# Revit family: IS_Iom_A7925_BIM_NL
name_source: partatom
category: Plumbing Fixtures
units: mm (PartAtom-declared; Revit-internal decimal feet)

## family parameters
Always vertical = No
Cut with Voids When Loaded = No
OmniClass Number = 23.45.05.14.21.11
OmniClass Title = Bath/Shower Units
Part Type = Normal
Room Calculation Point = No
Round Connector Dimension = Use Diameter
Shared = No
Work Plane-Based = No

## types (5) — shared parameters
Accessories = http://www.idealstandard.nl
Afmetingen = 76 x 107 x 218 mm
AfstandsEenheid = Millimeter
AreaUnits = millimetres
AssetType = Fixed
Auteur = Ideal Standard
BIMObjectName = IS_IdealStandard_SanitaryAccessories_IOM_A7925
BIMobject category = Sanitary: Toilet Accssories
BIMobject main category = Sanitary
BIMobject main category code = Sanitary
Beschrijvinggarantie = Herstellergarantie
Bestanddelen = http://www.idealstandard.nl
BimObjectNaam = IS_IdealStandard_SanitaryAccessories_IOM_A7925
Brand = Ideal Standard
Brand url = http://www.idealstandard.nl
Breedte = 76.032108
Category = Plumbing
Classification = Sanitary
ConnectionType = Plumbing
CurrencyUnit = €
CurrentRevision = 1
Date of publishing = 24/01/2023
Diepte = 107 mm
DurationUnit = Years
DuurEenheid = Jahr
Edition number = 1
ElementType = Sanitary Accessories
Garantieunits = Jahre
GemaaktOp = 24/01/2023
Help = http://www.idealstandard.nl
Hoogte = 218.007999420166
IFC Classification = Sanitary Terminal
IfcExportAs = IfcFurnitureType
IfcExportType = SOAP DISPENSER
Installatieinstructies = http://www.idealstandard.nl
Installation instructions = http://www.idealstandard.nl
InstallationInstructions = http://www.idealstandard.nl
Lengte = 107 mm
LinearUnits = millimeters
MaintenanceInformation = http://www.idealstandard.nl
Manufacturer = Ideal Standard
Manufacturer name = Ideal Standard
ManufacturerURL = http://www.idealstandard.nl
Materiaal = Messing&Stahl
Material = brass&steel
Material main = brass&steel
Merk = Ideal Standard
ModelReference = Iom Lotion Dispencer Wall Mounted
NBS Reference Code = 45-35-72/358
NBS Reference Description = Soap dispensers
Name = SanitaryAccessories_IOM_A7925_IdealStandard
NettWeight = 0.001
Nettogewicht = 0.001
NominalDepth = 107 mm
NominalHeight = 218 mm
NominalLength = 107 mm
NominalWidth = 76 mm
OppervlakteAfmeting = Millimeter
OppervlakteEenheid = Millimeter
PredefinedType = Sanitary Accessories
Product Guid = 11c9dca1-c7c1-4e85-bdf3-611bfd7340cd
Product SKU = A7925
Product certification = http://www.idealstandard.nl
Product data url = https://bimobject.com
Product family = Iom
Product group = Accessories
Product name = Iom Lotion Dispencer Wall Mounted
Product url = http://www.idealstandard.nl
ProductInformation = http://www.idealstandard.nl
Productinformatie = http://www.idealstandard.nl
QR code = http://bimobject.com
Revisie = 1
Shape = cilindrical
Size = 76 x 107 x 218 mm
Space = Internal
SpareParts = http://www.idealstandard.nl
Technical description = http://www.idealstandard.nl
Telefoonnummer = 077 355 08 08
Typeconnectie = Installation
UNSPSC Code = 30181500
URL = http://www.idealstandard.nl
Uniclass 1.4 Code = N14
Uniclass 1.4 Description = Accessories
Uniclass 2015 Code = Pr_40_20_76
Uniclass 2015 Name = Sanitary accessories
Uniclass2015Beschrijving = Sanitary accessories
Uniclass2015Code = Pr_40_20_76
Uniclass2015Referentie = Sanitary accessories
Uniclass2015Title = Sanitary accessories
Uniclass2015Version = V1.26
Uniformat II Code = C1030
Uniformat II Description = Fittings
Urlproducent = http://www.idealstandard.nl
ValutaEenheid = €
Versie = 1
Version = 1
VolumeUnits = Liters
Volumeunits = Liter
Vorm = Zylinder
WRASURL = https://www.wrasapprovals.co.uk
WarrantyDescription = Manufacturers Warranty
WarrantyDurationUnit = Years
Weight Net (Kg) = 0.001
Wisselstukken = http://www.idealstandard.nl
Youtube clip = https://www.youtube.com
zero-valued in all types: BrutoGewicht, Cost, Vervangingskosten

## per-type parameters (varying)
| type | Afwerking | Artikelnummer | Artikelomschrijving | BarCode | Color | Description | Features | Finish | GTIN code | Kleur | MainColor | Model | ModelNumber |
| A7925AA - Iom Lotion Dispencer Wall Mounted - Chrome | Chrom | A7925AA | Iom Lotionspender Wandmontage - Chrom | 4015413356251 | Chrome | Iom Lotion Dispencer Wall Mounted - Chrome | Lotion Dispencer Wall Mounted - Chrome | Chrome | 4015413356251 | Chrom | Chrome | A7925AA | A7925AA |
| A7925A2 - Iom Lotion Dispencer Wall Mounted - Brushed gold | Gebürstetes Gold | A7925A2 | Iom Lotionspender Wandmontage - Gebürstetes Gold | 4015413356268 | Brushed gold | Iom Lotion Dispencer Wall Mounted - Brushed gold | Lotion Dispencer Wall Mounted - Brushed gold | Brushed gold | 4015413356268 | Gebürstetes Gold | Brushed gold | A7925A2 | A7925A2 |
| A7925A5 - Iom Lotion Dispencer Wall Mounted - Magnetic grey | Magnetisch grau | A7925A5 | Iom Lotionspender Wandmontage - Magnetisch grau | 4015413356275 | Magnetic grey | Iom Lotion Dispencer Wall Mounted - Magnetic grey | Lotion Dispencer Wall Mounted - Magnetic grey | Magnetic grey | 4015413356275 | Magnetisch grau | Magnetic grey | A7925A5 | A7925A5 |
| A7925GN - Iom Lotion Dispencer Wall Mounted - Silver storm | Silbersturm | A7925GN | Iom Lotionsspender zur Wandmontage – Silberner Sturm | 4015413356282 | Silver storm | Iom Lotion Dispencer Wall Mounted - Silver storm | Lotion Dispencer Wall Mounted - Silver storm | Silver storm | 4015413356282 | Silberner Sturm | Silver storm | A7925GN | A7925GN |
| A7925XG - Iom Lotion Dispencer Wall Mounted - Silk Black | Seidenschwarz | A7925XG | Iom Lotionspender Wandmontage - Seidenschwarz | 4015413356299 | Silk Black | Iom Lotion Dispencer Wall Mounted - Silk Black | Lotion Dispencer Wall Mounted - Silk Black | Silk Black | 4015413356299 | Seidenschwarz | Silk Black | A7925XG | A7925XG |

## geometry (parser evidence)
native form markers: Sweep x3
no freeform markers — native parametric forms only
